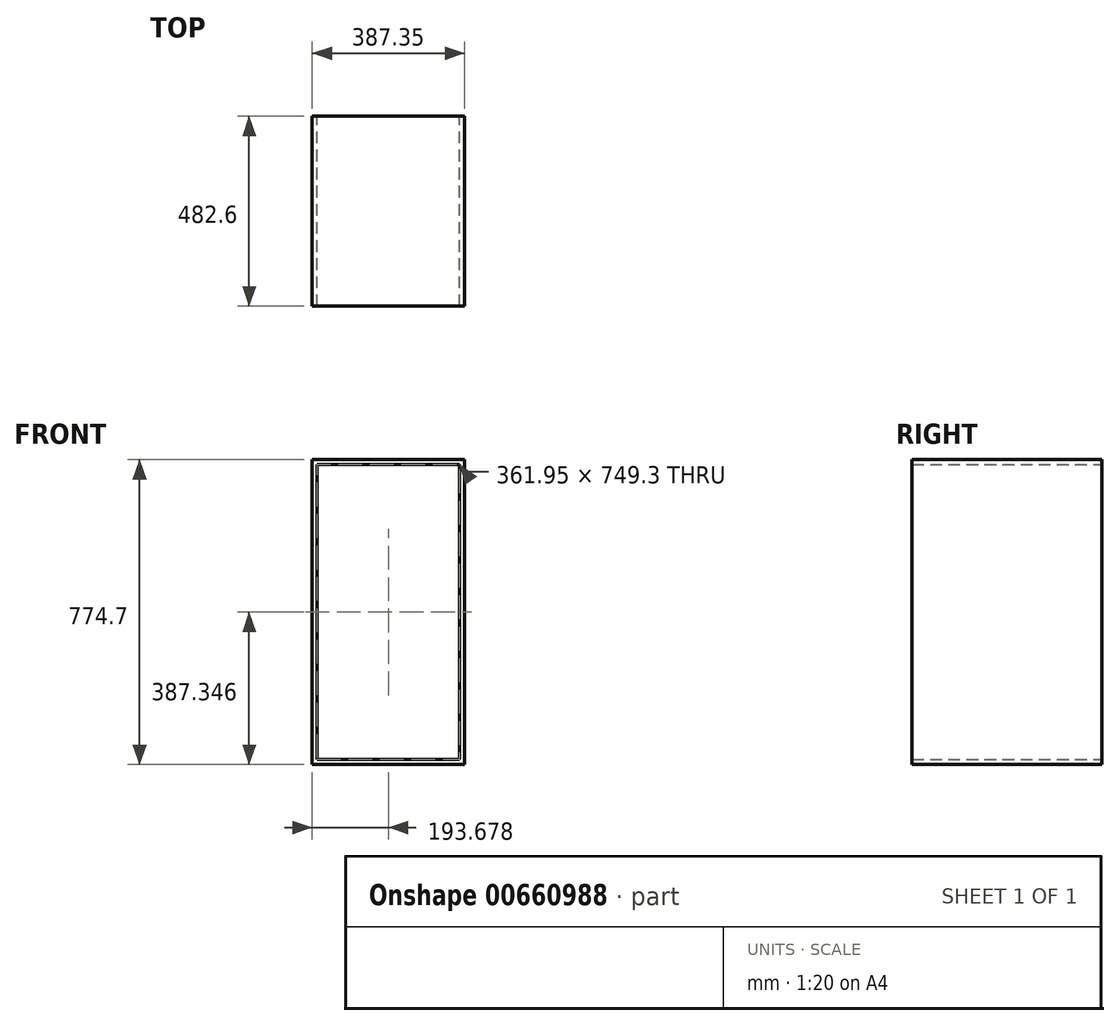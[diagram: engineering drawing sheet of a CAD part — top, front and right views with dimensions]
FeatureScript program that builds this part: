
annotation { "Feature Type Name" : "Feature", "Feature Type Description" : "" }
export const myFeature = defineFeature(function(context is Context, id is Id, definition is map)
    precondition{}
    {
        {
            var Q0;
            Q0=qCreatedBy(makeId("Front.planeOp"),FACE);
            var sketch = newSketch(context, id + "F0", { "sketchPlane" : qUnion([Q0])});
            skLineSegment(sketch, "E0.bottom", {"start": v(-315.22, 681.02) * mm, "end": v(46.73, 681.02) * mm});
            skLineSegment(sketch, "E0.top", {"start": v(-315.22, -68.28) * mm, "end": v(46.73, -68.28) * mm});
            skLineSegment(sketch, "E0.left", {"start": v(-315.22, 681.02) * mm, "end": v(-315.22, -68.28) * mm});
            skLineSegment(sketch, "E0.right", {"start": v(46.73, 681.02) * mm, "end": v(46.73, -68.28) * mm});
            skLineSegment(sketch, "E1.0", {"start": v(-327.92, 693.72) * mm, "end": v(59.43, 693.72) * mm});
            skLineSegment(sketch, "E1.1", {"start": v(-327.92, 693.72) * mm, "end": v(-327.92, -80.98) * mm});
            skLineSegment(sketch, "E1.2", {"start": v(-327.92, -80.98) * mm, "end": v(59.43, -80.98) * mm});
            skLineSegment(sketch, "E1.3", {"start": v(59.43, 693.72) * mm, "end": v(59.43, -80.98) * mm});
            skSolve(sketch);
        }
        {
            var Q0;
            Q0=makeQuery(id+"F0.imprint","IMPRINT",FACE,{"disambiguationData":[TD([[makeQuery(id+"F0.imprint","IMPRINT",EDGE,{"derivedFrom":sQuery(id+"F0.wireOp",EDGE,"E0.bottom")}),1.0]])]});
            extrude(context, id + "F1", {"entities" : qUnion([Q0]), "depth" : 482.6 * mm, "offsetDistance" : 25.4 * mm});
        }
    });
